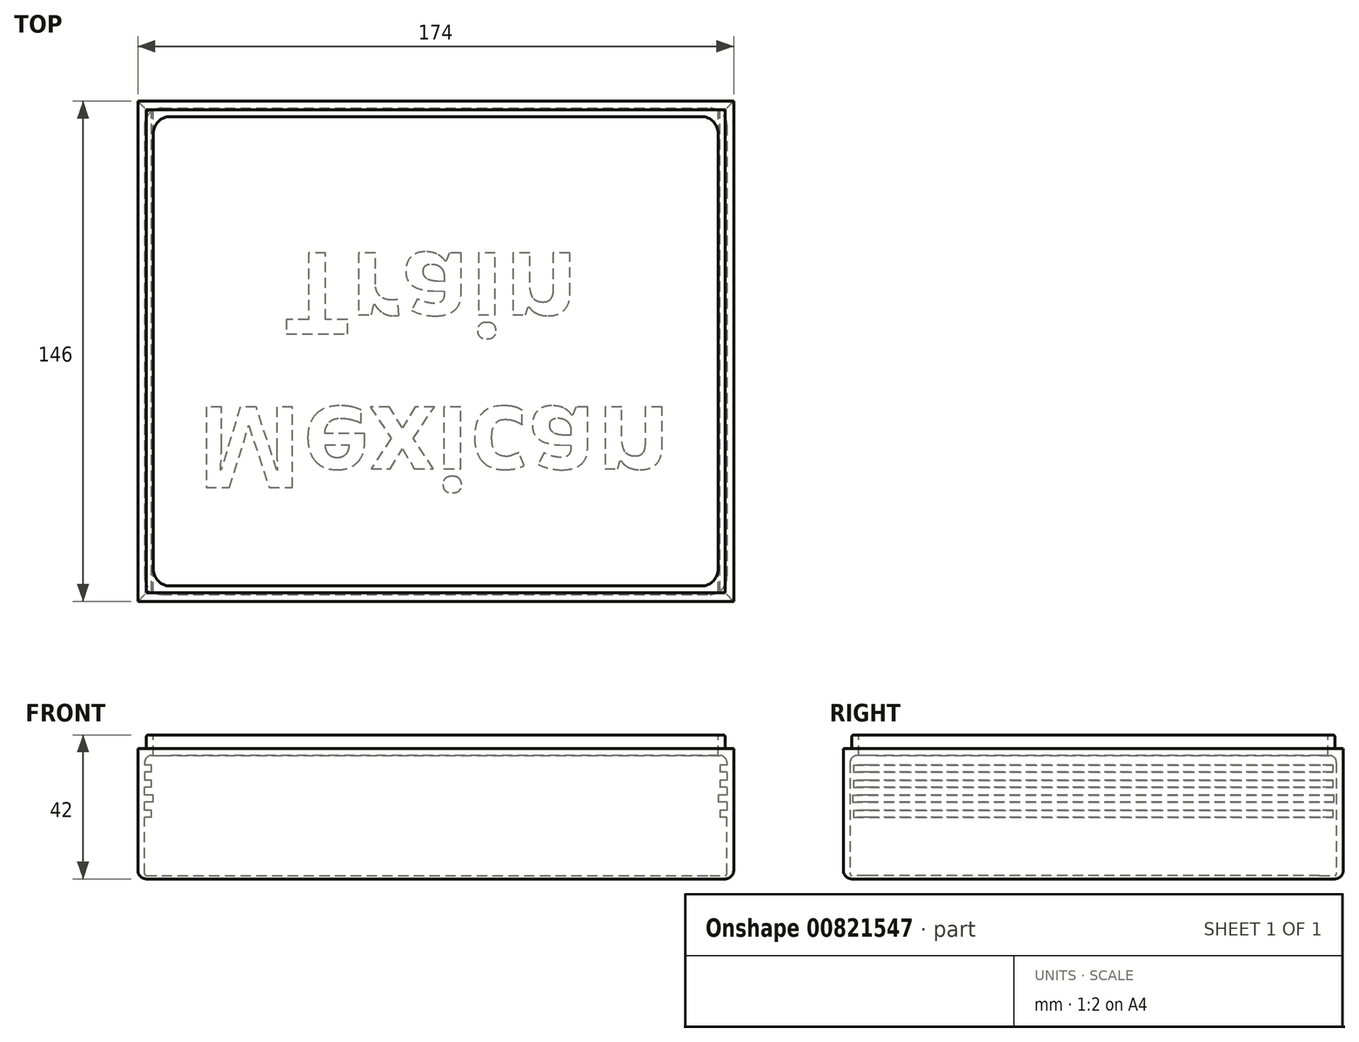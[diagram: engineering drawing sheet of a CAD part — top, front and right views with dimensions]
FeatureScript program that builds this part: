
annotation { "Feature Type Name" : "Feature", "Feature Type Description" : "" }
export const myFeature = defineFeature(function(context is Context, id is Id, definition is map)
    precondition{}
    {
        {
            var Q0;
            Q0=qCreatedBy(makeId("Top.planeOp"),FACE);
            var sketch = newSketch(context, id + "F0", { "sketchPlane" : qUnion([Q0])});
            skLineSegment(sketch, "E0.bottom", {"start": v(87, -73) * mm, "end": v(-87, -73) * mm});
            skLineSegment(sketch, "E0.top", {"start": v(87, 73) * mm, "end": v(-87, 73) * mm});
            skLineSegment(sketch, "E0.left", {"start": v(87, -73) * mm, "end": v(87, 73) * mm});
            skLineSegment(sketch, "E0.right", {"start": v(-87, -73) * mm, "end": v(-87, 73) * mm});
            skPoint(sketch, "E0.middle", {"position": v(0, 0) * mm});
            skLineSegment(sketch, "E1.bottom", {"start": v(85, -71) * mm, "end": v(-85, -71) * mm});
            skLineSegment(sketch, "E1.top", {"start": v(85, 71) * mm, "end": v(-85, 71) * mm});
            skLineSegment(sketch, "E1.left", {"start": v(85, -71) * mm, "end": v(85, 71) * mm});
            skLineSegment(sketch, "E1.right", {"start": v(-85, -71) * mm, "end": v(-85, 71) * mm});
            skSolve(sketch);
        }
        {
            var Q0;
            Q0=qSketchRegion(id+"F0",true);
            var Q1;
            Q1=makeQuery(id+"F0.imprint","IMPRINT",FACE,{"disambiguationData":[TD([[makeQuery(id+"F0.imprint","IMPRINT",EDGE,{"derivedFrom":sQuery(id+"F0.wireOp",EDGE,"E1.bottom")}),-1.0]])]});
            extrude(context, id + "F1", {"entities" : qUnion([Q0, Q1]), "depth" : 1 * mm, "offsetDistance" : 25 * mm});
        }
        {
            var Q0;
            Q0=makeQuery(id+"F0.imprint","IMPRINT",FACE,{"disambiguationData":[TD([[makeQuery(id+"F0.imprint","IMPRINT",EDGE,{"derivedFrom":sQuery(id+"F0.wireOp",EDGE,"E0.bottom")}),-1.0]])]});
            extrude(context, id + "F2", {"entities" : qUnion([Q0]), "operationType" : NewBodyOperationType.ADD, "depth" : 38 * mm, "offsetDistance" : 25 * mm});
        }
        {
            var Q0;
            {var subQ0=sQuery(id+"F0.wireOp",EDGE,"E0.bottom");Q0=makeQuery(id+"F2.boolean.opBoolean","MERGE",FACE,{"derivedFrom":[makeQuery(id+"F1.opExtrude","SWEPT_FACE",FACE,{"disambiguationData":[OSD([subQ0])]}),makeQuery(id+"F2.opExtrude","SWEPT_FACE",FACE,{"disambiguationData":[OSD([subQ0])]})]});}
            var sketch = newSketch(context, id + "F3", { "sketchPlane" : qUnion([Q0])});
            skLineSegment(sketch, "E2.bottom", {"start": v(-87, 20) * mm, "end": v(87, 20) * mm});
            skLineSegment(sketch, "E2.top", {"start": v(-87, 18) * mm, "end": v(87, 18) * mm});
            skLineSegment(sketch, "E2.left", {"start": v(-87, 20) * mm, "end": v(-87, 18) * mm});
            skLineSegment(sketch, "E2.right", {"start": v(87, 20) * mm, "end": v(87, 18) * mm});
            skLineSegment(sketch, "E3", {"start": v(-8.62, 0) * mm, "end": v(-8.62, 18) * mm, "construction": true});
            skLineSegment(sketch, "E4.bottom", {"start": v(-87, 22.2) * mm, "end": v(87, 22.2) * mm});
            skLineSegment(sketch, "E4.top", {"start": v(-87, 20.2) * mm, "end": v(87, 20.2) * mm});
            skLineSegment(sketch, "E4.left", {"start": v(-87, 22.2) * mm, "end": v(-87, 20.2) * mm});
            skLineSegment(sketch, "E4.right", {"start": v(87, 22.2) * mm, "end": v(87, 20.2) * mm});
            skLineSegment(sketch, "E5", {"start": v(-11.1, 20) * mm, "end": v(-11.1, 20.2) * mm, "construction": true});
            skLineSegment(sketch, "E6.bottom", {"start": v(-87, 24.4) * mm, "end": v(87, 24.4) * mm});
            skLineSegment(sketch, "E6.top", {"start": v(-87, 22.4) * mm, "end": v(87, 22.4) * mm});
            skLineSegment(sketch, "E6.left", {"start": v(-87, 24.4) * mm, "end": v(-87, 22.4) * mm});
            skLineSegment(sketch, "E6.right", {"start": v(87, 24.4) * mm, "end": v(87, 22.4) * mm});
            skLineSegment(sketch, "E7", {"start": v(-10.52, 22.2) * mm, "end": v(-10.52, 22.4) * mm, "construction": true});
            skLineSegment(sketch, "E8.bottom", {"start": v(-87, 26.6) * mm, "end": v(87, 26.6) * mm});
            skLineSegment(sketch, "E8.top", {"start": v(-87, 24.6) * mm, "end": v(87, 24.6) * mm});
            skLineSegment(sketch, "E8.left", {"start": v(-87, 26.6) * mm, "end": v(-87, 24.6) * mm});
            skLineSegment(sketch, "E8.right", {"start": v(87, 26.6) * mm, "end": v(87, 24.6) * mm});
            skLineSegment(sketch, "E9", {"start": v(-27.11, 24.6) * mm, "end": v(-27.11, 24.4) * mm, "construction": true});
            skLineSegment(sketch, "E10.bottom", {"start": v(-87, 28.8) * mm, "end": v(87, 28.8) * mm});
            skLineSegment(sketch, "E10.top", {"start": v(-87, 26.8) * mm, "end": v(87, 26.8) * mm});
            skLineSegment(sketch, "E10.left", {"start": v(-87, 28.8) * mm, "end": v(-87, 26.8) * mm});
            skLineSegment(sketch, "E10.right", {"start": v(87, 28.8) * mm, "end": v(87, 26.8) * mm});
            skLineSegment(sketch, "E11.bottom", {"start": v(-87, 31) * mm, "end": v(87, 31) * mm});
            skLineSegment(sketch, "E11.top", {"start": v(-87, 29) * mm, "end": v(87, 29) * mm});
            skLineSegment(sketch, "E11.left", {"start": v(-87, 31) * mm, "end": v(-87, 29) * mm});
            skLineSegment(sketch, "E11.right", {"start": v(87, 31) * mm, "end": v(87, 29) * mm});
            skLineSegment(sketch, "E12", {"start": v(-29.7, 26.6) * mm, "end": v(-29.7, 26.8) * mm, "construction": true});
            skLineSegment(sketch, "E13", {"start": v(-28.43, 28.8) * mm, "end": v(-28.43, 29) * mm, "construction": true});
            skLineSegment(sketch, "E14.bottom", {"start": v(-87, 33.2) * mm, "end": v(87, 33.2) * mm});
            skLineSegment(sketch, "E14.top", {"start": v(-87, 31.2) * mm, "end": v(87, 31.2) * mm});
            skLineSegment(sketch, "E14.left", {"start": v(-87, 33.2) * mm, "end": v(-87, 31.2) * mm});
            skLineSegment(sketch, "E14.right", {"start": v(87, 33.2) * mm, "end": v(87, 31.2) * mm});
            skLineSegment(sketch, "E15", {"start": v(-34.63, 31) * mm, "end": v(-34.63, 31.2) * mm, "construction": true});
            skLineSegment(sketch, "E16.bottom", {"start": v(-87, 38) * mm, "end": v(87, 38) * mm});
            skLineSegment(sketch, "E16.top", {"start": v(-87, 36) * mm, "end": v(87, 36) * mm});
            skLineSegment(sketch, "E16.left", {"start": v(-87, 38) * mm, "end": v(-87, 36) * mm});
            skLineSegment(sketch, "E16.right", {"start": v(87, 38) * mm, "end": v(87, 36) * mm});
            skSolve(sketch);
        }
        {
            var Q0;
            Q0=makeQuery(id+"F3.imprint","IMPRINT",FACE,{"disambiguationData":[TD([[makeQuery(id+"F3.imprint","IMPRINT",EDGE,{"derivedFrom":sQuery(id+"F3.wireOp",EDGE,"E2.bottom")}),-1.0]])]});
            extrude(context, id + "F4", {"entities" : qUnion([Q0]), "operationType" : NewBodyOperationType.ADD, "oppositeDirection" : true, "depth" : 146 * mm, "offsetDistance" : 25 * mm});
        }
        {
            var Q0;
            Q0=makeQuery(id+"F4.opExtrude","SWEPT_FACE",FACE,{"disambiguationData":[OSD([sQuery(id+"F3.wireOp",EDGE,"E2.bottom")])]});
            var sketch = newSketch(context, id + "F5", { "sketchPlane" : qUnion([Q0])});
            skLineSegment(sketch, "E17.bottom", {"start": v(83, -71) * mm, "end": v(-83, -71) * mm});
            skLineSegment(sketch, "E17.top", {"start": v(83, 71) * mm, "end": v(-83, 71) * mm});
            skLineSegment(sketch, "E17.left", {"start": v(83, -71) * mm, "end": v(83, 71) * mm});
            skLineSegment(sketch, "E17.right", {"start": v(-83, -71) * mm, "end": v(-83, 71) * mm});
            skPoint(sketch, "E17.middle", {"position": v(0, 0) * mm});
            skSolve(sketch);
        }
        {
            var Q0;
            Q0=makeQuery(id+"F5.imprint","IMPRINT",FACE,{"disambiguationData":[TD([[makeQuery(id+"F5.imprint","IMPRINT",EDGE,{"derivedFrom":sQuery(id+"F5.wireOp",EDGE,"E17.bottom")}),1.0]])]});
            extrude(context, id + "F6", {"entities" : qUnion([Q0]), "operationType" : NewBodyOperationType.REMOVE, "oppositeDirection" : true, "depth" : 2 * mm, "offsetDistance" : 25 * mm});
        }
        {
            var Q0;
            Q0=makeQuery(id+"F3.imprint","IMPRINT",FACE,{"disambiguationData":[TD([[makeQuery(id+"F3.imprint","IMPRINT",EDGE,{"derivedFrom":sQuery(id+"F3.wireOp",EDGE,"E6.bottom")}),-1.0]])]});
            extrude(context, id + "F7", {"entities" : qUnion([Q0]), "operationType" : NewBodyOperationType.ADD, "oppositeDirection" : true, "depth" : 146 * mm, "offsetDistance" : 25 * mm});
        }
        {
            var Q0;
            Q0=makeQuery(id+"F7.opExtrude","SWEPT_FACE",FACE,{"disambiguationData":[OSD([sQuery(id+"F3.wireOp",EDGE,"E6.bottom")])]});
            var sketch = newSketch(context, id + "F8", { "sketchPlane" : qUnion([Q0])});
            skLineSegment(sketch, "E18.bottom", {"start": v(82.5, -71) * mm, "end": v(-82.5, -71) * mm});
            skLineSegment(sketch, "E18.top", {"start": v(82.5, 71) * mm, "end": v(-82.5, 71) * mm});
            skLineSegment(sketch, "E18.left", {"start": v(82.5, -71) * mm, "end": v(82.5, 71) * mm});
            skLineSegment(sketch, "E18.right", {"start": v(-82.5, -71) * mm, "end": v(-82.5, 71) * mm});
            skPoint(sketch, "E18.middle", {"position": v(0, 0) * mm});
            skSolve(sketch);
        }
        {
            var Q0;
            {var subQ0=sQuery(id+"F8.wireOp",EDGE,"E18.left");var subQ1=makeQuery(id+"F7.opExtrude","SWEPT_FACE",FACE,{"disambiguationData":[OSD([sQuery(id+"F3.wireOp",EDGE,"E6.bottom")])]});var subQ2=sQuery(id+"F3.wireOp",EDGE,"E4.bottom");var subQ3=sQuery(id+"F0.wireOp",EDGE,"E1.bottom");var subQ9=makeQuery(id+"F4.opExtrude","SWEPT_FACE",FACE,{"disambiguationData":[OSD([sQuery(id+"F3.wireOp",EDGE,"E2.bottom")])]});var subQ12=makeQuery(id+"F4.boolean.opBoolean","SPLIT",FACE,{"disambiguationData":[TD([subQ9])],"derivedFrom":makeQuery(id+"F2.opExtrude","SWEPT_FACE",FACE,{"disambiguationData":[OSD([subQ3])]})});var subQ13=makeQuery(id+"F9g47IUq5KTh1mP_1.opExtrude","SWEPT_FACE",FACE,{"disambiguationData":[OSD([subQ2])]});var subQ14=makeQuery(id+"F7.boolean.opBoolean","INTERSECT",EDGE,{"derivedFrom":[makeQuery(id+"FOzXX6xhWMd1yj7_1.boolean.opBoolean","MERGE",FACE,{"derivedFrom":[makeQuery(id+"F9g47IUq5KTh1mP_1.boolean.opBoolean","SPLIT",FACE,{"disambiguationData":[TD([subQ13])],"derivedFrom":subQ12}),makeQuery(id+"F9g47IUq5KTh1mP_1.boolean.opBoolean","SPLIT",FACE,{"disambiguationData":[TD([subQ9])],"derivedFrom":subQ12}),makeQuery(id+"FOzXX6xhWMd1yj7_1.opExtrude","SWEPT_FACE",FACE,{"disambiguationData":[OSD([subQ3,subQ2])]})]}),subQ1]});var subQ15=makeQuery(id+"F8.imprint","INTERSECT",VERTEX,{"derivedFrom":[subQ14,subQ0]});Q0=makeQuery(id+"F8.imprint","IMPRINT",FACE,{"disambiguationData":[TD([[makeQuery(id+"F8.imprint","IMPRINT",EDGE,{"disambiguationData":[TD([[subQ15,-1.0]])],"derivedFrom":subQ0}),1.0]])]});}
            extrude(context, id + "F9", {"entities" : qUnion([Q0]), "operationType" : NewBodyOperationType.REMOVE, "oppositeDirection" : true, "depth" : 2 * mm, "offsetDistance" : 25 * mm});
        }
        {
            var Q0;
            Q0=makeQuery(id+"F3.imprint","IMPRINT",FACE,{"disambiguationData":[TD([[makeQuery(id+"F3.imprint","IMPRINT",EDGE,{"derivedFrom":sQuery(id+"F3.wireOp",EDGE,"E10.bottom")}),-1.0]])]});
            extrude(context, id + "F10", {"entities" : qUnion([Q0]), "operationType" : NewBodyOperationType.ADD, "oppositeDirection" : true, "depth" : 146 * mm, "offsetDistance" : 25 * mm});
        }
        {
            var Q0;
            Q0=makeQuery(id+"F10.opExtrude","SWEPT_FACE",FACE,{"disambiguationData":[OSD([sQuery(id+"F3.wireOp",EDGE,"E10.bottom")])]});
            var sketch = newSketch(context, id + "F11", { "sketchPlane" : qUnion([Q0])});
            skLineSegment(sketch, "E19.bottom", {"start": v(-83, -71) * mm, "end": v(83, -71) * mm});
            skLineSegment(sketch, "E19.top", {"start": v(-83, 71) * mm, "end": v(83, 71) * mm});
            skLineSegment(sketch, "E19.left", {"start": v(-83, -71) * mm, "end": v(-83, 71) * mm});
            skLineSegment(sketch, "E19.right", {"start": v(83, -71) * mm, "end": v(83, 71) * mm});
            skPoint(sketch, "E19.middle", {"position": v(0, 0) * mm});
            skSolve(sketch);
        }
        {
            var Q0;
            Q0=makeQuery(id+"F11.imprint","IMPRINT",FACE,{"disambiguationData":[TD([[makeQuery(id+"F11.imprint","IMPRINT",EDGE,{"derivedFrom":sQuery(id+"F11.wireOp",EDGE,"E19.bottom")}),1.0]])]});
            extrude(context, id + "F12", {"entities" : qUnion([Q0]), "operationType" : NewBodyOperationType.REMOVE, "oppositeDirection" : true, "depth" : 2 * mm, "offsetDistance" : 25 * mm});
        }
        {
            var Q0;
            Q0=makeQuery(id+"F3.imprint","IMPRINT",FACE,{"disambiguationData":[TD([[makeQuery(id+"F3.imprint","IMPRINT",EDGE,{"derivedFrom":sQuery(id+"F3.wireOp",EDGE,"E11.bottom")}),-1.0]])]});
            extrude(context, id + "F13", {"entities" : qUnion([Q0]), "operationType" : NewBodyOperationType.ADD, "oppositeDirection" : true, "depth" : 146 * mm, "offsetDistance" : 25 * mm});
        }
        {
            var Q0;
            Q0=makeQuery(id+"F13.opExtrude","SWEPT_FACE",FACE,{"disambiguationData":[OSD([sQuery(id+"F3.wireOp",EDGE,"E11.bottom")])]});
            var sketch = newSketch(context, id + "F14", { "sketchPlane" : qUnion([Q0])});
            skLineSegment(sketch, "E20.bottom", {"start": v(84.5, -70.5) * mm, "end": v(-84.5, -70.5) * mm});
            skLineSegment(sketch, "E20.top", {"start": v(84.5, 70.5) * mm, "end": v(-84.5, 70.5) * mm});
            skLineSegment(sketch, "E20.left", {"start": v(84.5, -70.5) * mm, "end": v(84.5, 70.5) * mm});
            skLineSegment(sketch, "E20.right", {"start": v(-84.5, -70.5) * mm, "end": v(-84.5, 70.5) * mm});
            skSolve(sketch);
        }
        {
            var Q0;
            Q0=makeQuery(id+"F14.imprint","IMPRINT",FACE,{"disambiguationData":[TD([[makeQuery(id+"F14.imprint","IMPRINT",EDGE,{"derivedFrom":sQuery(id+"F14.wireOp",EDGE,"E20.bottom")}),1.0]])]});
            var Q1;
            Q1=makeQuery(id+"F14.imprint","IMPRINT",FACE,{"disambiguationData":[TD([[makeQuery(id+"F14.imprint","IMPRINT",EDGE,{"derivedFrom":sQuery(id+"F14.wireOp",EDGE,"E20.bottom")}),-1.0]])]});
            extrude(context, id + "F15", {"entities" : qUnion([Q0, Q1]), "operationType" : NewBodyOperationType.REMOVE, "oppositeDirection" : true, "depth" : 2 * mm, "offsetDistance" : 25 * mm});
        }
        {
            var Q0;
            Q0=makeQuery(id+"F3.imprint","IMPRINT",FACE,{"disambiguationData":[TD([[makeQuery(id+"F3.imprint","IMPRINT",EDGE,{"derivedFrom":sQuery(id+"F3.wireOp",EDGE,"E14.bottom")}),-1.0]])]});
            extrude(context, id + "F16", {"entities" : qUnion([Q0]), "operationType" : NewBodyOperationType.ADD, "oppositeDirection" : true, "depth" : 146 * mm, "offsetDistance" : 25 * mm});
        }
        {
            var Q0;
            Q0=makeQuery(id+"F16.opExtrude","SWEPT_FACE",FACE,{"disambiguationData":[OSD([sQuery(id+"F3.wireOp",EDGE,"E14.bottom")])]});
            var sketch = newSketch(context, id + "F17", { "sketchPlane" : qUnion([Q0])});
            skLineSegment(sketch, "E21.bottom", {"start": v(83, -71) * mm, "end": v(-83, -71) * mm});
            skLineSegment(sketch, "E21.top", {"start": v(83, 71) * mm, "end": v(-83, 71) * mm});
            skLineSegment(sketch, "E21.left", {"start": v(83, -71) * mm, "end": v(83, 71) * mm});
            skLineSegment(sketch, "E21.right", {"start": v(-83, -71) * mm, "end": v(-83, 71) * mm});
            skPoint(sketch, "E21.middle", {"position": v(0, 0) * mm});
            skSolve(sketch);
        }
        {
            var Q0;
            Q0=makeQuery(id+"F17.imprint","IMPRINT",FACE,{"disambiguationData":[TD([[makeQuery(id+"F17.imprint","IMPRINT",EDGE,{"derivedFrom":sQuery(id+"F17.wireOp",EDGE,"E21.bottom")}),1.0]])]});
            extrude(context, id + "F18", {"entities" : qUnion([Q0]), "operationType" : NewBodyOperationType.REMOVE, "oppositeDirection" : true, "depth" : 2 * mm, "offsetDistance" : 25 * mm});
        }
        {
            var Q0;
            Q0=makeQuery(id+"F3.imprint","IMPRINT",FACE,{"disambiguationData":[TD([[makeQuery(id+"F3.imprint","IMPRINT",EDGE,{"derivedFrom":sQuery(id+"F3.wireOp",EDGE,"E16.bottom")}),1.0]])]});
            extrude(context, id + "F19", {"entities" : qUnion([Q0]), "operationType" : NewBodyOperationType.ADD, "oppositeDirection" : true, "depth" : 146 * mm, "offsetDistance" : 25 * mm});
        }
        {
            var Q0;
            Q0=makeQuery(id+"F19.boolean.opBoolean","MERGE",FACE,{"derivedFrom":[makeQuery(id+"F2.opExtrude","CAP_FACE",FACE,{"disambiguationData":[OSD([sQuery(id+"F0.wireOp",EDGE,"E0.bottom"),sQuery(id+"F0.wireOp",EDGE,"E0.top"),sQuery(id+"F0.wireOp",EDGE,"E0.left"),sQuery(id+"F0.wireOp",EDGE,"E0.right"),sQuery(id+"F0.wireOp",EDGE,"E1.bottom"),sQuery(id+"F0.wireOp",EDGE,"E1.top"),sQuery(id+"F0.wireOp",EDGE,"E1.left"),sQuery(id+"F0.wireOp",EDGE,"E1.right")])],"isStart":false}),makeQuery(id+"F19.opExtrude","SWEPT_FACE",FACE,{"disambiguationData":[OSD([sQuery(id+"F3.wireOp",EDGE,"E16.bottom")])]})]});
            var sketch = newSketch(context, id + "F20", { "sketchPlane" : qUnion([Q0])});
            skLineSegment(sketch, "E22.bottom", {"start": v(82.5, -68.5) * mm, "end": v(-82.5, -68.5) * mm});
            skLineSegment(sketch, "E22.top", {"start": v(82.5, 68.5) * mm, "end": v(-82.5, 68.5) * mm});
            skLineSegment(sketch, "E22.left", {"start": v(82.5, -68.5) * mm, "end": v(82.5, 68.5) * mm});
            skLineSegment(sketch, "E22.right", {"start": v(-82.5, -68.5) * mm, "end": v(-82.5, 68.5) * mm});
            skPoint(sketch, "E22.middle", {"position": v(0, 0) * mm});
            skSolve(sketch);
        }
        {
            var Q0;
            Q0=makeQuery(id+"F20.imprint","IMPRINT",FACE,{"disambiguationData":[TD([[makeQuery(id+"F20.imprint","IMPRINT",EDGE,{"derivedFrom":sQuery(id+"F20.wireOp",EDGE,"E22.bottom")}),-1.0]])]});
            extrude(context, id + "F21", {"entities" : qUnion([Q0]), "operationType" : NewBodyOperationType.REMOVE, "oppositeDirection" : true, "depth" : 2 * mm, "offsetDistance" : 25 * mm});
        }
        {
            var Q0;
            Q0=makeQuery(id+"F19.boolean.opBoolean","MERGE",FACE,{"derivedFrom":[makeQuery(id+"F2.opExtrude","CAP_FACE",FACE,{"disambiguationData":[OSD([sQuery(id+"F0.wireOp",EDGE,"E0.bottom"),sQuery(id+"F0.wireOp",EDGE,"E0.top"),sQuery(id+"F0.wireOp",EDGE,"E0.left"),sQuery(id+"F0.wireOp",EDGE,"E0.right"),sQuery(id+"F0.wireOp",EDGE,"E1.bottom"),sQuery(id+"F0.wireOp",EDGE,"E1.top"),sQuery(id+"F0.wireOp",EDGE,"E1.left"),sQuery(id+"F0.wireOp",EDGE,"E1.right")])],"isStart":false}),makeQuery(id+"F19.opExtrude","SWEPT_FACE",FACE,{"disambiguationData":[OSD([sQuery(id+"F3.wireOp",EDGE,"E16.bottom")])]})]});
            var sketch = newSketch(context, id + "F22", { "sketchPlane" : qUnion([Q0])});
            skLineSegment(sketch, "E23.bottom", {"start": v(84.5, -70.5) * mm, "end": v(-84.5, -70.5) * mm});
            skLineSegment(sketch, "E23.top", {"start": v(84.5, 70.5) * mm, "end": v(-84.5, 70.5) * mm});
            skLineSegment(sketch, "E23.left", {"start": v(84.5, -70.5) * mm, "end": v(84.5, 70.5) * mm});
            skLineSegment(sketch, "E23.right", {"start": v(-84.5, -70.5) * mm, "end": v(-84.5, 70.5) * mm});
            skPoint(sketch, "E23.middle", {"position": v(0, 0) * mm});
            skSolve(sketch);
        }
        {
            var Q0;
            Q0=makeQuery(id+"F22.imprint","IMPRINT",FACE,{"disambiguationData":[TD([[makeQuery(id+"F22.imprint","IMPRINT",EDGE,{"derivedFrom":sQuery(id+"F22.wireOp",EDGE,"E23.bottom")}),-1.0]])]});
            extrude(context, id + "F23", {"entities" : qUnion([Q0]), "operationType" : NewBodyOperationType.ADD, "depth" : 4 * mm, "offsetDistance" : 25 * mm});
        }
        {
            var Q0;
            {var subQ0=sQuery(id+"F3.wireOp",EDGE,"E8.bottom");var subQ1=sQuery(id+"F3.wireOp",EDGE,"E4.bottom");var subQ2=sQuery(id+"F0.wireOp",EDGE,"E1.right");var subQ4=sQuery(id+"F8.wireOp",EDGE,"E18.top");var subQ6=sQuery(id+"F5.wireOp",EDGE,"E17.top");var subQ7=sQuery(id+"F0.wireOp",EDGE,"E1.top");var subQ9=sQuery(id+"FCqpddPiBGxFMdr_1.wireOp",EDGE,"liuN6yKZ-wBV1-jaHT-AlhS-nctVBK3Vym5k.bottom");var subQ12=sQuery(id+"F11.wireOp",EDGE,"E19.top");var subQ15=sQuery(id+"F3.wireOp",EDGE,"E11.bottom");var subQ19=makeQuery(id+"F10.opExtrude","SWEPT_FACE",FACE,{"disambiguationData":[OSD([sQuery(id+"F3.wireOp",EDGE,"E10.bottom")])]});var subQ20=makeQuery(id+"F7.opExtrude","SWEPT_FACE",FACE,{"disambiguationData":[OSD([sQuery(id+"F3.wireOp",EDGE,"E6.bottom")])]});var subQ21=makeQuery(id+"F4.opExtrude","SWEPT_FACE",FACE,{"disambiguationData":[OSD([sQuery(id+"F3.wireOp",EDGE,"E2.bottom")])]});var subQ22=makeQuery(id+"F4.boolean.opBoolean","SPLIT",EDGE,{"disambiguationData":[TD([subQ21])],"derivedFrom":makeQuery(id+"F2.opExtrude","SWEPT_EDGE",EDGE,{"disambiguationData":[OSD([subQ7,subQ2])]})});var subQ23=makeQuery(id+"F7.boolean.opBoolean","SPLIT",EDGE,{"disambiguationData":[TD([subQ20])],"derivedFrom":makeQuery(id+"FOzXX6xhWMd1yj7_1.boolean.opBoolean","MERGE",EDGE,{"derivedFrom":[makeQuery(id+"F9g47IUq5KTh1mP_1.boolean.opBoolean","SPLIT",EDGE,{"disambiguationData":[TD([makeQuery(id+"F9g47IUq5KTh1mP_1.opExtrude","SWEPT_FACE",FACE,{"disambiguationData":[OSD([subQ1])]})])],"derivedFrom":subQ22}),makeQuery(id+"F9g47IUq5KTh1mP_1.boolean.opBoolean","SPLIT",EDGE,{"disambiguationData":[TD([subQ21])],"derivedFrom":subQ22}),makeQuery(id+"FOzXX6xhWMd1yj7_1.opExtrude","SWEPT_EDGE",EDGE,{"disambiguationData":[OSD([subQ7,subQ2,subQ1,subQ6])]})]})});var subQ24=makeQuery(id+"F10.boolean.opBoolean","SPLIT",EDGE,{"disambiguationData":[TD([subQ19])],"derivedFrom":makeQuery(id+"FV3jQboMJTqKbcJ_1.boolean.opBoolean","MERGE",EDGE,{"derivedFrom":[makeQuery(id+"F7hxh2N4XlYWTVC_1.boolean.opBoolean","SPLIT",EDGE,{"disambiguationData":[TD([makeQuery(id+"F7hxh2N4XlYWTVC_1.opExtrude","SWEPT_FACE",FACE,{"disambiguationData":[OSD([subQ0])]})])],"derivedFrom":subQ23}),makeQuery(id+"F7hxh2N4XlYWTVC_1.boolean.opBoolean","SPLIT",EDGE,{"disambiguationData":[TD([subQ20])],"derivedFrom":subQ23}),makeQuery(id+"FV3jQboMJTqKbcJ_1.opExtrude","SWEPT_EDGE",EDGE,{"disambiguationData":[OSD([subQ7,subQ2,subQ1,subQ0,subQ6,subQ4])]})]})});Q0=makeQuery(id+"F16.boolean.opBoolean","SPLIT",EDGE,{"disambiguationData":[TD([makeQuery(id+"F16.opExtrude","SWEPT_FACE",FACE,{"disambiguationData":[OSD([sQuery(id+"F3.wireOp",EDGE,"E14.bottom")])]})])],"derivedFrom":makeQuery(id+"F15.boolean.opBoolean","MERGE",EDGE,{"derivedFrom":[makeQuery(id+"F13.boolean.opBoolean","SPLIT",EDGE,{"disambiguationData":[TD([makeQuery(id+"F13.opExtrude","SWEPT_FACE",FACE,{"disambiguationData":[OSD([subQ15])]})])],"derivedFrom":subQ24}),makeQuery(id+"F13.boolean.opBoolean","SPLIT",EDGE,{"disambiguationData":[TD([subQ19])],"derivedFrom":subQ24}),makeQuery(id+"F15.opExtrude","SWEPT_EDGE",EDGE,{"disambiguationData":[OSD([subQ7,subQ2,subQ1,subQ0,subQ15,subQ6,subQ4,subQ9,subQ12])]})]})});}
            var Q1;
            {var subQ0=sQuery(id+"F20.wireOp",EDGE,"E22.right");var subQ1=sQuery(id+"F20.wireOp",EDGE,"E22.top");Q1=makeQuery(id+"F23.boolean.opBoolean","MERGE",EDGE,{"derivedFrom":[makeQuery(id+"F21.boolean.opBoolean","COPY",EDGE,{"derivedFrom":makeQuery(id+"F21.opExtrude","SWEPT_EDGE",EDGE,{"disambiguationData":[OSD([subQ1,subQ0])]})}),makeQuery(id+"F23.opExtrude","SWEPT_EDGE",EDGE,{"disambiguationData":[OSD([subQ1,subQ0])]})]});}
            var Q2;
            {var subQ0=sQuery(id+"F11.wireOp",EDGE,"E19.top");var subQ2=sQuery(id+"F8.wireOp",EDGE,"E18.top");var subQ4=sQuery(id+"F3.wireOp",EDGE,"E8.bottom");var subQ5=sQuery(id+"F3.wireOp",EDGE,"E4.bottom");var subQ6=sQuery(id+"F0.wireOp",EDGE,"E1.left");var subQ8=sQuery(id+"F0.wireOp",EDGE,"E1.top");var subQ10=sQuery(id+"F5.wireOp",EDGE,"E17.top");var subQ13=sQuery(id+"FCqpddPiBGxFMdr_1.wireOp",EDGE,"liuN6yKZ-wBV1-jaHT-AlhS-nctVBK3Vym5k.bottom");var subQ18=sQuery(id+"F3.wireOp",EDGE,"E11.bottom");var subQ19=makeQuery(id+"F10.opExtrude","SWEPT_FACE",FACE,{"disambiguationData":[OSD([sQuery(id+"F3.wireOp",EDGE,"E10.bottom")])]});var subQ20=makeQuery(id+"F7.opExtrude","SWEPT_FACE",FACE,{"disambiguationData":[OSD([sQuery(id+"F3.wireOp",EDGE,"E6.bottom")])]});var subQ21=makeQuery(id+"F4.opExtrude","SWEPT_FACE",FACE,{"disambiguationData":[OSD([sQuery(id+"F3.wireOp",EDGE,"E2.bottom")])]});var subQ22=makeQuery(id+"F4.boolean.opBoolean","SPLIT",EDGE,{"disambiguationData":[TD([subQ21])],"derivedFrom":makeQuery(id+"F2.opExtrude","SWEPT_EDGE",EDGE,{"disambiguationData":[OSD([subQ8,subQ6])]})});var subQ23=makeQuery(id+"F7.boolean.opBoolean","SPLIT",EDGE,{"disambiguationData":[TD([subQ20])],"derivedFrom":makeQuery(id+"FOzXX6xhWMd1yj7_1.boolean.opBoolean","MERGE",EDGE,{"derivedFrom":[makeQuery(id+"F9g47IUq5KTh1mP_1.boolean.opBoolean","SPLIT",EDGE,{"disambiguationData":[TD([makeQuery(id+"F9g47IUq5KTh1mP_1.opExtrude","SWEPT_FACE",FACE,{"disambiguationData":[OSD([subQ5])]})])],"derivedFrom":subQ22}),makeQuery(id+"F9g47IUq5KTh1mP_1.boolean.opBoolean","SPLIT",EDGE,{"disambiguationData":[TD([subQ21])],"derivedFrom":subQ22}),makeQuery(id+"FOzXX6xhWMd1yj7_1.opExtrude","SWEPT_EDGE",EDGE,{"disambiguationData":[OSD([subQ8,subQ6,subQ5,subQ10])]})]})});var subQ24=makeQuery(id+"F10.boolean.opBoolean","SPLIT",EDGE,{"disambiguationData":[TD([subQ19])],"derivedFrom":makeQuery(id+"FV3jQboMJTqKbcJ_1.boolean.opBoolean","MERGE",EDGE,{"derivedFrom":[makeQuery(id+"F7hxh2N4XlYWTVC_1.boolean.opBoolean","SPLIT",EDGE,{"disambiguationData":[TD([makeQuery(id+"F7hxh2N4XlYWTVC_1.opExtrude","SWEPT_FACE",FACE,{"disambiguationData":[OSD([subQ4])]})])],"derivedFrom":subQ23}),makeQuery(id+"F7hxh2N4XlYWTVC_1.boolean.opBoolean","SPLIT",EDGE,{"disambiguationData":[TD([subQ20])],"derivedFrom":subQ23}),makeQuery(id+"FV3jQboMJTqKbcJ_1.opExtrude","SWEPT_EDGE",EDGE,{"disambiguationData":[OSD([subQ8,subQ6,subQ5,subQ4,subQ10,subQ2])]})]})});Q2=makeQuery(id+"F16.boolean.opBoolean","SPLIT",EDGE,{"disambiguationData":[TD([makeQuery(id+"F16.opExtrude","SWEPT_FACE",FACE,{"disambiguationData":[OSD([sQuery(id+"F3.wireOp",EDGE,"E14.bottom")])]})])],"derivedFrom":makeQuery(id+"F15.boolean.opBoolean","MERGE",EDGE,{"derivedFrom":[makeQuery(id+"F13.boolean.opBoolean","SPLIT",EDGE,{"disambiguationData":[TD([makeQuery(id+"F13.opExtrude","SWEPT_FACE",FACE,{"disambiguationData":[OSD([subQ18])]})])],"derivedFrom":subQ24}),makeQuery(id+"F13.boolean.opBoolean","SPLIT",EDGE,{"disambiguationData":[TD([subQ19])],"derivedFrom":subQ24}),makeQuery(id+"F15.opExtrude","SWEPT_EDGE",EDGE,{"disambiguationData":[OSD([subQ8,subQ6,subQ5,subQ4,subQ18,subQ10,subQ2,subQ13,subQ0])]})]})});}
            var Q3;
            {var subQ0=sQuery(id+"F20.wireOp",EDGE,"E22.left");var subQ1=sQuery(id+"F20.wireOp",EDGE,"E22.top");Q3=makeQuery(id+"F23.boolean.opBoolean","MERGE",EDGE,{"derivedFrom":[makeQuery(id+"F21.boolean.opBoolean","COPY",EDGE,{"derivedFrom":makeQuery(id+"F21.opExtrude","SWEPT_EDGE",EDGE,{"disambiguationData":[OSD([subQ1,subQ0])]})}),makeQuery(id+"F23.opExtrude","SWEPT_EDGE",EDGE,{"disambiguationData":[OSD([subQ1,subQ0])]})]});}
            var Q4;
            {var subQ0=sQuery(id+"F20.wireOp",EDGE,"E22.left");var subQ1=sQuery(id+"F20.wireOp",EDGE,"E22.bottom");Q4=makeQuery(id+"F23.boolean.opBoolean","MERGE",EDGE,{"derivedFrom":[makeQuery(id+"F21.boolean.opBoolean","COPY",EDGE,{"derivedFrom":makeQuery(id+"F21.opExtrude","SWEPT_EDGE",EDGE,{"disambiguationData":[OSD([subQ1,subQ0])]})}),makeQuery(id+"F23.opExtrude","SWEPT_EDGE",EDGE,{"disambiguationData":[OSD([subQ1,subQ0])]})]});}
            var Q5;
            {var subQ0=makeQuery(id+"F10.opExtrude","SWEPT_FACE",FACE,{"disambiguationData":[OSD([sQuery(id+"F3.wireOp",EDGE,"E10.bottom")])]});var subQ1=sQuery(id+"FCqpddPiBGxFMdr_1.wireOp",EDGE,"wBCVjx1v-jUHT-JwVk-Ksni-hv4pDAcsEu1o.bottom");var subQ2=sQuery(id+"F8.wireOp",EDGE,"E18.bottom");var subQ3=sQuery(id+"F5.wireOp",EDGE,"E17.bottom");var subQ4=sQuery(id+"F3.wireOp",EDGE,"E8.bottom");var subQ5=sQuery(id+"F3.wireOp",EDGE,"E4.bottom");var subQ6=sQuery(id+"F0.wireOp",EDGE,"E1.bottom");var subQ10=sQuery(id+"F11.wireOp",EDGE,"E19.bottom");var subQ13=sQuery(id+"F3.wireOp",EDGE,"E11.bottom");var subQ14=sQuery(id+"F0.wireOp",EDGE,"E1.left");var subQ20=makeQuery(id+"F7.opExtrude","SWEPT_FACE",FACE,{"disambiguationData":[OSD([sQuery(id+"F3.wireOp",EDGE,"E6.bottom")])]});var subQ21=makeQuery(id+"F4.opExtrude","SWEPT_FACE",FACE,{"disambiguationData":[OSD([sQuery(id+"F3.wireOp",EDGE,"E2.bottom")])]});var subQ22=makeQuery(id+"F4.boolean.opBoolean","SPLIT",EDGE,{"disambiguationData":[TD([subQ21])],"derivedFrom":makeQuery(id+"F2.opExtrude","SWEPT_EDGE",EDGE,{"disambiguationData":[OSD([subQ6,subQ14])]})});var subQ23=makeQuery(id+"F7.boolean.opBoolean","SPLIT",EDGE,{"disambiguationData":[TD([subQ20])],"derivedFrom":makeQuery(id+"FOzXX6xhWMd1yj7_1.boolean.opBoolean","MERGE",EDGE,{"derivedFrom":[makeQuery(id+"F9g47IUq5KTh1mP_1.boolean.opBoolean","SPLIT",EDGE,{"disambiguationData":[TD([makeQuery(id+"F9g47IUq5KTh1mP_1.opExtrude","SWEPT_FACE",FACE,{"disambiguationData":[OSD([subQ5])]})])],"derivedFrom":subQ22}),makeQuery(id+"F9g47IUq5KTh1mP_1.boolean.opBoolean","SPLIT",EDGE,{"disambiguationData":[TD([subQ21])],"derivedFrom":subQ22}),makeQuery(id+"FOzXX6xhWMd1yj7_1.opExtrude","SWEPT_EDGE",EDGE,{"disambiguationData":[OSD([subQ6,subQ14,subQ5,subQ3])]})]})});var subQ24=makeQuery(id+"F10.boolean.opBoolean","SPLIT",EDGE,{"disambiguationData":[TD([subQ0])],"derivedFrom":makeQuery(id+"FV3jQboMJTqKbcJ_1.boolean.opBoolean","MERGE",EDGE,{"derivedFrom":[makeQuery(id+"F7hxh2N4XlYWTVC_1.boolean.opBoolean","SPLIT",EDGE,{"disambiguationData":[TD([makeQuery(id+"F7hxh2N4XlYWTVC_1.opExtrude","SWEPT_FACE",FACE,{"disambiguationData":[OSD([subQ4])]})])],"derivedFrom":subQ23}),makeQuery(id+"F7hxh2N4XlYWTVC_1.boolean.opBoolean","SPLIT",EDGE,{"disambiguationData":[TD([subQ20])],"derivedFrom":subQ23}),makeQuery(id+"FV3jQboMJTqKbcJ_1.opExtrude","SWEPT_EDGE",EDGE,{"disambiguationData":[OSD([subQ6,subQ14,subQ5,subQ4,subQ3,subQ2])]})]})});Q5=makeQuery(id+"F16.boolean.opBoolean","SPLIT",EDGE,{"disambiguationData":[TD([subQ0])],"derivedFrom":makeQuery(id+"F15.boolean.opBoolean","MERGE",EDGE,{"derivedFrom":[makeQuery(id+"F13.boolean.opBoolean","SPLIT",EDGE,{"disambiguationData":[TD([makeQuery(id+"F13.opExtrude","SWEPT_FACE",FACE,{"disambiguationData":[OSD([subQ13])]})])],"derivedFrom":subQ24}),makeQuery(id+"F13.boolean.opBoolean","SPLIT",EDGE,{"disambiguationData":[TD([subQ0])],"derivedFrom":subQ24}),makeQuery(id+"F15.opExtrude","SWEPT_EDGE",EDGE,{"disambiguationData":[OSD([subQ6,subQ14,subQ5,subQ4,subQ13,subQ3,subQ2,subQ1,subQ10])]})]})});}
            var Q6;
            {var subQ0=makeQuery(id+"F10.opExtrude","SWEPT_FACE",FACE,{"disambiguationData":[OSD([sQuery(id+"F3.wireOp",EDGE,"E10.bottom")])]});var subQ1=sQuery(id+"F3.wireOp",EDGE,"E8.bottom");var subQ2=sQuery(id+"F3.wireOp",EDGE,"E4.bottom");var subQ3=sQuery(id+"F0.wireOp",EDGE,"E1.right");var subQ5=sQuery(id+"F11.wireOp",EDGE,"E19.bottom");var subQ6=sQuery(id+"FCqpddPiBGxFMdr_1.wireOp",EDGE,"wBCVjx1v-jUHT-JwVk-Ksni-hv4pDAcsEu1o.bottom");var subQ7=sQuery(id+"F8.wireOp",EDGE,"E18.bottom");var subQ8=sQuery(id+"F5.wireOp",EDGE,"E17.bottom");var subQ9=sQuery(id+"F3.wireOp",EDGE,"E11.bottom");var subQ10=sQuery(id+"F0.wireOp",EDGE,"E1.bottom");var subQ20=makeQuery(id+"F7.opExtrude","SWEPT_FACE",FACE,{"disambiguationData":[OSD([sQuery(id+"F3.wireOp",EDGE,"E6.bottom")])]});var subQ21=makeQuery(id+"F4.opExtrude","SWEPT_FACE",FACE,{"disambiguationData":[OSD([sQuery(id+"F3.wireOp",EDGE,"E2.bottom")])]});var subQ22=makeQuery(id+"F4.boolean.opBoolean","SPLIT",EDGE,{"disambiguationData":[TD([subQ21])],"derivedFrom":makeQuery(id+"F2.opExtrude","SWEPT_EDGE",EDGE,{"disambiguationData":[OSD([subQ10,subQ3])]})});var subQ23=makeQuery(id+"F7.boolean.opBoolean","SPLIT",EDGE,{"disambiguationData":[TD([subQ20])],"derivedFrom":makeQuery(id+"FOzXX6xhWMd1yj7_1.boolean.opBoolean","MERGE",EDGE,{"derivedFrom":[makeQuery(id+"F9g47IUq5KTh1mP_1.boolean.opBoolean","SPLIT",EDGE,{"disambiguationData":[TD([makeQuery(id+"F9g47IUq5KTh1mP_1.opExtrude","SWEPT_FACE",FACE,{"disambiguationData":[OSD([subQ2])]})])],"derivedFrom":subQ22}),makeQuery(id+"F9g47IUq5KTh1mP_1.boolean.opBoolean","SPLIT",EDGE,{"disambiguationData":[TD([subQ21])],"derivedFrom":subQ22}),makeQuery(id+"FOzXX6xhWMd1yj7_1.opExtrude","SWEPT_EDGE",EDGE,{"disambiguationData":[OSD([subQ10,subQ3,subQ2,subQ8])]})]})});var subQ24=makeQuery(id+"F10.boolean.opBoolean","SPLIT",EDGE,{"disambiguationData":[TD([subQ0])],"derivedFrom":makeQuery(id+"FV3jQboMJTqKbcJ_1.boolean.opBoolean","MERGE",EDGE,{"derivedFrom":[makeQuery(id+"F7hxh2N4XlYWTVC_1.boolean.opBoolean","SPLIT",EDGE,{"disambiguationData":[TD([makeQuery(id+"F7hxh2N4XlYWTVC_1.opExtrude","SWEPT_FACE",FACE,{"disambiguationData":[OSD([subQ1])]})])],"derivedFrom":subQ23}),makeQuery(id+"F7hxh2N4XlYWTVC_1.boolean.opBoolean","SPLIT",EDGE,{"disambiguationData":[TD([subQ20])],"derivedFrom":subQ23}),makeQuery(id+"FV3jQboMJTqKbcJ_1.opExtrude","SWEPT_EDGE",EDGE,{"disambiguationData":[OSD([subQ10,subQ3,subQ2,subQ1,subQ8,subQ7])]})]})});Q6=makeQuery(id+"F16.boolean.opBoolean","SPLIT",EDGE,{"disambiguationData":[TD([subQ0])],"derivedFrom":makeQuery(id+"F15.boolean.opBoolean","MERGE",EDGE,{"derivedFrom":[makeQuery(id+"F13.boolean.opBoolean","SPLIT",EDGE,{"disambiguationData":[TD([makeQuery(id+"F13.opExtrude","SWEPT_FACE",FACE,{"disambiguationData":[OSD([subQ9])]})])],"derivedFrom":subQ24}),makeQuery(id+"F13.boolean.opBoolean","SPLIT",EDGE,{"disambiguationData":[TD([subQ0])],"derivedFrom":subQ24}),makeQuery(id+"F15.opExtrude","SWEPT_EDGE",EDGE,{"disambiguationData":[OSD([subQ10,subQ3,subQ2,subQ1,subQ9,subQ8,subQ7,subQ6,subQ5])]})]})});}
            var Q7;
            {var subQ0=sQuery(id+"F20.wireOp",EDGE,"E22.right");var subQ1=sQuery(id+"F20.wireOp",EDGE,"E22.bottom");Q7=makeQuery(id+"F23.boolean.opBoolean","MERGE",EDGE,{"derivedFrom":[makeQuery(id+"F21.boolean.opBoolean","COPY",EDGE,{"derivedFrom":makeQuery(id+"F21.opExtrude","SWEPT_EDGE",EDGE,{"disambiguationData":[OSD([subQ1,subQ0])]})}),makeQuery(id+"F23.opExtrude","SWEPT_EDGE",EDGE,{"disambiguationData":[OSD([subQ1,subQ0])]})]});}
            fillet(context, id + "F24", {"entities" : qUnion([Q0, Q1, Q2, Q3, Q4, Q5, Q6, Q7]), "radius" : 5 * mm, "tangentPropagation" : true, "allowEdgeOverflow" : false});
        }
        {
            var Q0;
            Q0=makeQuery(id+"F23.opExtrude","CAP_FACE",FACE,{"disambiguationData":[OSD([sQuery(id+"F20.wireOp",EDGE,"E22.bottom"),sQuery(id+"F20.wireOp",EDGE,"E22.top"),sQuery(id+"F20.wireOp",EDGE,"E22.left"),sQuery(id+"F20.wireOp",EDGE,"E22.right"),sQuery(id+"F22.wireOp",EDGE,"E23.bottom"),sQuery(id+"F22.wireOp",EDGE,"E23.top"),sQuery(id+"F22.wireOp",EDGE,"E23.left"),sQuery(id+"F22.wireOp",EDGE,"E23.right")])],"isStart":false});
            var Q1;
            Q1=makeQuery(id+"F1.opExtrude","CAP_FACE",FACE,{"disambiguationData":[OSD([sQuery(id+"F0.wireOp",EDGE,"E0.bottom"),sQuery(id+"F0.wireOp",EDGE,"E0.top"),sQuery(id+"F0.wireOp",EDGE,"E0.left"),sQuery(id+"F0.wireOp",EDGE,"E0.right")])],"isStart":false});
            fillet(context, id + "F25", {"entities" : qUnion([Q0, Q1]), "radius" : .5 * mm, "tangentPropagation" : true, "allowEdgeOverflow" : false});
        }
        {
            var Q0;
            Q0=makeQuery(id+"F1.opExtrude","CAP_FACE",FACE,{"disambiguationData":[OSD([sQuery(id+"F0.wireOp",EDGE,"E0.bottom"),sQuery(id+"F0.wireOp",EDGE,"E0.top"),sQuery(id+"F0.wireOp",EDGE,"E0.left"),sQuery(id+"F0.wireOp",EDGE,"E0.right")])],"isStart":true});
            fillet(context, id + "F26", {"entities" : qUnion([Q0]), "radius" : 2.5 * mm, "tangentPropagation" : true, "allowEdgeOverflow" : false});
        }
        {
            var Q0;
            Q0=makeQuery(id+"F1.opExtrude","CAP_FACE",FACE,{"disambiguationData":[OSD([sQuery(id+"F0.wireOp",EDGE,"E0.bottom"),sQuery(id+"F0.wireOp",EDGE,"E0.top"),sQuery(id+"F0.wireOp",EDGE,"E0.left"),sQuery(id+"F0.wireOp",EDGE,"E0.right")])],"isStart":true});
            var sketch = newSketch(context, id + "F27", { "sketchPlane" : qUnion([Q0])});
            skText(sketch, "E24", { "text": "Mexican\n   Train", "fontName": "OpenSans-Bold.ttf"});
            skLineSegment(sketch, "E25", {"start": v(0, 0) * mm, "end": v(0, 40) * mm, "construction": true});
            skLineSegment(sketch, "E26", {"start": v(0, 40) * mm, "end": v(-70, 40) * mm, "construction": true});
            const initialGuessF27  = {"E24": [-0.07, 0.01621, 1, 0, 0.02379]};
            skSetInitialGuess(sketch, initialGuessF27);
            skSolve(sketch);
        }
        {
            var Q0;
            Q0=qSketchRegion(id+"F27",true);
            extrude(context, id + "F28", {"entities" : qUnion([Q0]), "operationType" : NewBodyOperationType.REMOVE, "oppositeDirection" : true, "depth" : .1 * mm, "offsetDistance" : 25 * mm});
        }
        {
            var Q0;
            {var subQ3=sQuery(id+"F3.wireOp",EDGE,"E8.bottom");var subQ4=sQuery(id+"F3.wireOp",EDGE,"E4.bottom");var subQ12=sQuery(id+"F0.wireOp",EDGE,"E1.right");var subQ26=sQuery(id+"F3.wireOp",EDGE,"E11.bottom");var subQ27=makeQuery(id+"F10.opExtrude","SWEPT_FACE",FACE,{"disambiguationData":[OSD([sQuery(id+"F3.wireOp",EDGE,"E10.bottom")])]});var subQ28=makeQuery(id+"F7.opExtrude","SWEPT_FACE",FACE,{"disambiguationData":[OSD([sQuery(id+"F3.wireOp",EDGE,"E6.bottom")])]});var subQ29=makeQuery(id+"F4.opExtrude","SWEPT_FACE",FACE,{"disambiguationData":[OSD([sQuery(id+"F3.wireOp",EDGE,"E2.bottom")])]});var subQ30=makeQuery(id+"F4.boolean.opBoolean","SPLIT",FACE,{"disambiguationData":[TD([subQ29])],"derivedFrom":makeQuery(id+"F2.opExtrude","SWEPT_FACE",FACE,{"disambiguationData":[OSD([subQ12])]})});var subQ31=makeQuery(id+"F7.boolean.opBoolean","SPLIT",FACE,{"disambiguationData":[TD([subQ28])],"derivedFrom":makeQuery(id+"FOzXX6xhWMd1yj7_1.boolean.opBoolean","MERGE",FACE,{"derivedFrom":[makeQuery(id+"F9g47IUq5KTh1mP_1.boolean.opBoolean","SPLIT",FACE,{"disambiguationData":[TD([makeQuery(id+"F9g47IUq5KTh1mP_1.opExtrude","SWEPT_FACE",FACE,{"disambiguationData":[OSD([subQ4])]})])],"derivedFrom":subQ30}),makeQuery(id+"F9g47IUq5KTh1mP_1.boolean.opBoolean","SPLIT",FACE,{"disambiguationData":[TD([subQ29])],"derivedFrom":subQ30}),makeQuery(id+"FOzXX6xhWMd1yj7_1.opExtrude","SWEPT_FACE",FACE,{"disambiguationData":[OSD([subQ12,subQ4])]})]})});var subQ32=makeQuery(id+"F10.boolean.opBoolean","SPLIT",FACE,{"disambiguationData":[TD([subQ27])],"derivedFrom":makeQuery(id+"FV3jQboMJTqKbcJ_1.boolean.opBoolean","MERGE",FACE,{"derivedFrom":[makeQuery(id+"F7hxh2N4XlYWTVC_1.boolean.opBoolean","SPLIT",FACE,{"disambiguationData":[TD([makeQuery(id+"F7hxh2N4XlYWTVC_1.opExtrude","SWEPT_FACE",FACE,{"disambiguationData":[OSD([subQ3])]})])],"derivedFrom":subQ31}),makeQuery(id+"F7hxh2N4XlYWTVC_1.boolean.opBoolean","SPLIT",FACE,{"disambiguationData":[TD([subQ28])],"derivedFrom":subQ31}),makeQuery(id+"FV3jQboMJTqKbcJ_1.opExtrude","SWEPT_FACE",FACE,{"disambiguationData":[OSD([subQ12,subQ4,subQ3])]})]})});Q0=makeQuery(id+"F19.boolean.opBoolean","INTERSECT",EDGE,{"derivedFrom":[makeQuery(id+"F16.boolean.opBoolean","SPLIT",FACE,{"disambiguationData":[TD([makeQuery(id+"F16.opExtrude","SWEPT_FACE",FACE,{"disambiguationData":[OSD([sQuery(id+"F3.wireOp",EDGE,"E14.bottom")])]})])],"derivedFrom":makeQuery(id+"F15.boolean.opBoolean","MERGE",FACE,{"derivedFrom":[makeQuery(id+"F13.boolean.opBoolean","SPLIT",FACE,{"disambiguationData":[TD([makeQuery(id+"F13.opExtrude","SWEPT_FACE",FACE,{"disambiguationData":[OSD([subQ26])]})])],"derivedFrom":subQ32}),makeQuery(id+"F13.boolean.opBoolean","SPLIT",FACE,{"disambiguationData":[TD([subQ27])],"derivedFrom":subQ32}),makeQuery(id+"F15.opExtrude","SWEPT_FACE",FACE,{"disambiguationData":[OSD([subQ12,subQ4,subQ3,subQ26])]})]})}),makeQuery(id+"F19.opExtrude","SWEPT_FACE",FACE,{"disambiguationData":[OSD([sQuery(id+"F3.wireOp",EDGE,"E16.top")])]})]});}
            fillet(context, id + "F29", {"entities" : qUnion([Q0]), "radius" : 2 * mm, "tangentPropagation" : true, "allowEdgeOverflow" : false});
        }
    });
